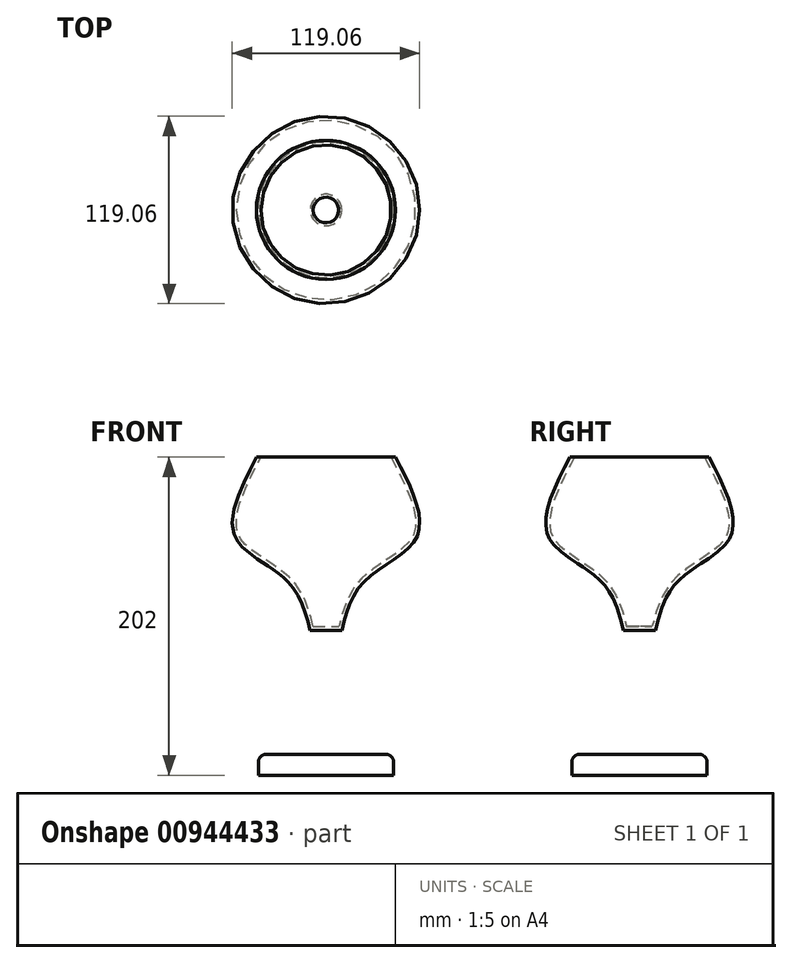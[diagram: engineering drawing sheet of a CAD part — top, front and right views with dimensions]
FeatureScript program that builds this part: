
annotation { "Feature Type Name" : "Feature", "Feature Type Description" : "" }
export const myFeature = defineFeature(function(context is Context, id is Id, definition is map)
    precondition{}
    {
        {
            var Q0;
            Q0=qCreatedBy(makeId("Top.planeOp"),FACE);
            var sketch = newSketch(context, id + "F0", { "sketchPlane" : qUnion([Q0])});
            skCircle(sketch, "E0", {"center": v(0, 0) * mm, "radius": 10.04 * mm});
            skSolve(sketch);
        }
        {
            var Q0;
            Q0=qCreatedBy(makeId("Top.planeOp"),FACE);
            cPlane(context, id + "F1", {"entities" : qUnion([Q0]), "cplaneType" : CPlaneType.OFFSET, "offset" : 110 * mm, "width" : 152.4 * mm, "height" : 152.4 * mm});
        }
        {
            var Q0;
            Q0=qCreatedBy(id+"F1.planeOp",FACE);
            var sketch = newSketch(context, id + "F2", { "sketchPlane" : qUnion([Q0])});
            skCircle(sketch, "E1", {"center": v(0, 0) * mm, "radius": 44.2 * mm});
            skSolve(sketch);
        }
        {
            var Q0;
            Q0=qCreatedBy(makeId("Top.planeOp"),FACE);
            cPlane(context, id + "F3", {"entities" : qUnion([Q0]), "cplaneType" : CPlaneType.OFFSET, "offset" : 29 * mm, "width" : 150 * mm, "height" : 150 * mm});
        }
        {
            var Q0;
            Q0=qCreatedBy(makeId("Top.planeOp"),FACE);
            cPlane(context, id + "F4", {"entities" : qUnion([Q0]), "cplaneType" : CPlaneType.OFFSET, "offset" : 58 * mm, "width" : 150 * mm, "height" : 150 * mm});
        }
        {
            var Q0;
            Q0=qCreatedBy(id+"F4.planeOp",FACE);
            var sketch = newSketch(context, id + "F5", { "sketchPlane" : qUnion([Q0])});
            skCircle(sketch, "E2", {"center": v(0, 0) * mm, "radius": 57.02 * mm});
            skSolve(sketch);
        }
        {
            var Q0;
            Q0=qCreatedBy(id+"F3.planeOp",FACE);
            var sketch = newSketch(context, id + "F6", { "sketchPlane" : qUnion([Q0])});
            skCircle(sketch, "E3", {"center": v(0, 0) * mm, "radius": 22.35 * mm});
            skSolve(sketch);
        }
        {
            var Q0;
            Q0=makeQuery(id+"F0.imprint","IMPRINT",FACE,{"disambiguationData":[TD([[makeQuery(id+"F0.imprint","IMPRINT",EDGE,{"derivedFrom":sQuery(id+"F0.wireOp",EDGE,"E0")}),1.0]])]});
            var Q1;
            Q1=makeQuery(id+"F6.imprint","IMPRINT",FACE,{"disambiguationData":[TD([[makeQuery(id+"F6.imprint","IMPRINT",EDGE,{"derivedFrom":sQuery(id+"F6.wireOp",EDGE,"E3")}),1.0]])]});
            var Q2;
            Q2=makeQuery(id+"F5.imprint","IMPRINT",FACE,{"disambiguationData":[TD([[makeQuery(id+"F5.imprint","IMPRINT",EDGE,{"derivedFrom":sQuery(id+"F5.wireOp",EDGE,"E2")}),1.0]])]});
            var Q3;
            Q3=makeQuery(id+"F2.imprint","IMPRINT",FACE,{"disambiguationData":[TD([[makeQuery(id+"F2.imprint","IMPRINT",EDGE,{"derivedFrom":sQuery(id+"F2.wireOp",EDGE,"E1")}),1.0]])]});
            loft(context, id + "F7", {"sheetProfilesArray" : [{ "sheetProfileEntities" : qUnion([Q0]) }, { "sheetProfileEntities" : qUnion([Q1]) }, { "sheetProfileEntities" : qUnion([Q2]) }, { "sheetProfileEntities" : qUnion([Q3]) }]});
        }
        {
            var Q0;
            Q0=qCreatedBy(makeId("Top.planeOp"),FACE);
            cPlane(context, id + "F8", {"entities" : qUnion([Q0]), "cplaneType" : CPlaneType.OFFSET, "offset" : 81 * mm, "oppositeDirection" : true, "width" : 150 * mm, "height" : 150 * mm});
        }
        {
            var Q0;
            Q0=qCreatedBy(id+"F8.planeOp",FACE);
            var sketch = newSketch(context, id + "F9", { "sketchPlane" : qUnion([Q0])});
            skCircle(sketch, "E4", {"center": v(0, 0) * mm, "radius": 10.23 * mm});
            skSolve(sketch);
        }
        {
            var Q0;
            Q0=sQuery(id+"F9.wireOp",EDGE,"E4");
            var Q1;
            Q1=makeQuery(id+"F7.opLoft","MID_CAP_EDGE",EDGE,{"disambiguationData":[OSD([sQuery(id+"F0.wireOp",EDGE,"E0")])],"capPos":0.0});
            loft(context, id + "F10", {"bodyType" : ToolBodyType.SURFACE, "wireProfilesArray" : [{ "wireProfileEntities" : qUnion([Q0]) }, { "wireProfileEntities" : qUnion([Q1]) }]});
        }
        {
            var Q0;
            Q0=qCreatedBy(id+"F8.planeOp",FACE);
            cPlane(context, id + "F11", {"entities" : qUnion([Q0]), "cplaneType" : CPlaneType.OFFSET, "offset" : 11 * mm, "oppositeDirection" : true, "width" : 150 * mm, "height" : 150 * mm});
        }
        {
            var Q0;
            Q0=qCreatedBy(id+"F11.planeOp",FACE);
            var sketch = newSketch(context, id + "F12", { "sketchPlane" : qUnion([Q0])});
            skCircle(sketch, "E5", {"center": v(0, 0) * mm, "radius": 42.92 * mm});
            skSolve(sketch);
        }
        {
            var Q0;
            Q0=qSketchRegion(id+"F12",true);
            extrude(context, id + "F13", {"entities" : qUnion([Q0]), "depth" : 13.3 * mm, "offsetDistance" : 25 * mm});
        }
        {
            var Q0;
            Q0=makeQuery(id+"F13.opExtrude","CAP_EDGE",EDGE,{"disambiguationData":[OSD([sQuery(id+"F12.wireOp",EDGE,"E5")])],"isStart":false});
            fillet(context, id + "F14", {"entities" : qUnion([Q0]), "radius" : 5 * mm, "tangentPropagation" : true, "allowEdgeOverflow" : false});
        }
        {
            var Q0;
            Q0=makeQuery(id+"F7.opLoft","CAP_FACE",FACE,{"disambiguationData":[OSD([makeQuery(id+"F2.imprint","IMPRINT",FACE,{"disambiguationData":[TD([[makeQuery(id+"F2.imprint","IMPRINT",EDGE,{"derivedFrom":sQuery(id+"F2.wireOp",EDGE,"E1")}),1.0]])]})])],"isStart":true});
            shell(context, id + "F15", {"entities" : qUnion([Q0]), "thickness" : 2.5 * mm});
        }
    });
